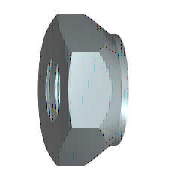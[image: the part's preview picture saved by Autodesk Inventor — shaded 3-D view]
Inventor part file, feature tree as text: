
AUTODESK INVENTOR PART (.ipt)
format: ipt  version: 2017 (Build 210142000, 142)  size: 185,344 bytes
history: native  units: mm (DEFAULTED — no unit token found)
features: sketch x3, hole x1, chamfer x1, other x1, plane x1
ambient origin geometry x7: Origin, YZ Plane, XZ Plane, X Axis, Y Axis, Z Axis, Center Point
bodies: Solid1 (feature_tree), Body (feature_tree)
feature tree (7):
  hole  "Thread"  [1 undecoded]
  chamfer  "Chamfer3"  Distance=5.5mm
  other  "Work Axis1"
  plane  "Work Plane1"
  sketch  "Sketch1"  dims[d0=6.350853mm d1=3.1mm]
  sketch  "Sketch3"  dims[d3=30.0deg d5=5.5mm d6=4.675mm d7=90.0deg d8=8.726646mm d9=1.4mm d24=2.459mm d25=6.0mm d26=4.0mm d27=2.0mm d28=14.3117mm d29=8.0mm d30=20.594885mm d10=0.270633mm d11=30.0deg d12=0.270633mm d13=30.0deg d14=0.0mm d38=0.0mm d39=0.270633mm d40=0.270633mm d41=0.0mm d42=0.0mm]
  sketch  "Sketch2"  dims[d2=0.0mm]
note: 1 required parameter value undecoded (feature->parameter linkage not recoverable at this tier; creation-order binding heuristic only, values carry confidence <= 0.55)
